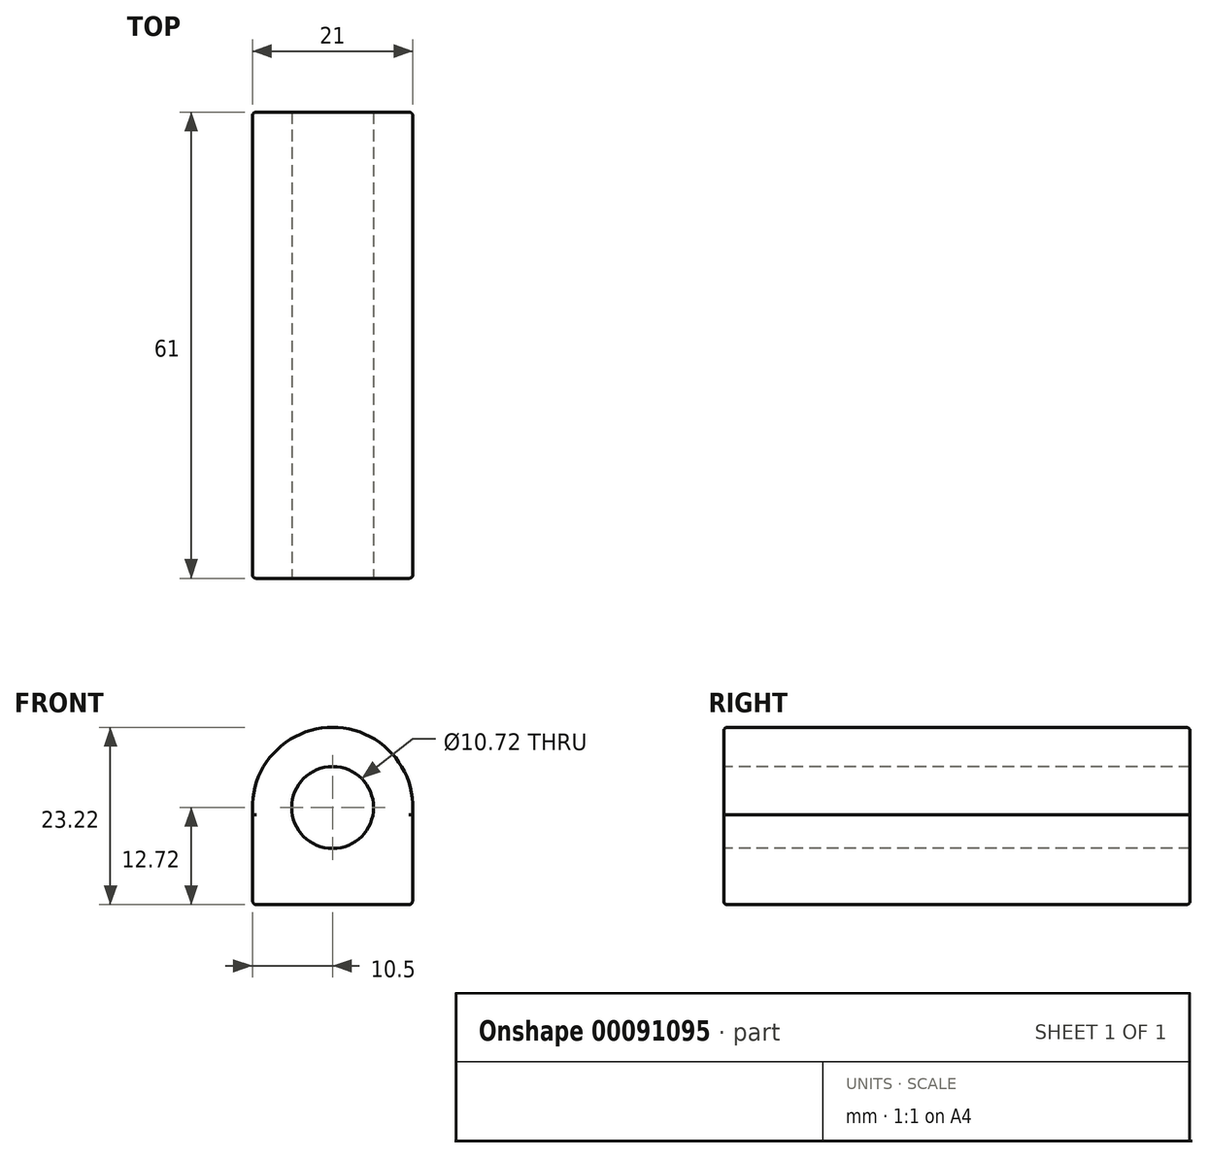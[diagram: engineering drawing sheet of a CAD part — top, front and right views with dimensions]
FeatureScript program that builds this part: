
annotation { "Feature Type Name" : "Feature", "Feature Type Description" : "" }
export const myFeature = defineFeature(function(context is Context, id is Id, definition is map)
    precondition{}
    {
        {
            var Q0;
            Q0=qCreatedBy(makeId("Front.planeOp"),FACE);
            var sketch = newSketch(context, id + "F0", { "sketchPlane" : qUnion([Q0])});
            skCircle(sketch, "E0", {"center": v(0, 0) * mm, "radius": 10.5 * mm});
            skLineSegment(sketch, "E1", {"start": v(0, 0) * mm, "end": v(0, -10.5) * mm, "construction": true});
            skLineSegment(sketch, "E2", {"start": v(0, -5.25) * mm, "end": v(-9.1, -5.25) * mm, "construction": true});
            skLineSegment(sketch, "E3.bottom", {"start": v(10.46, -10.72) * mm, "end": v(-10.46, -10.72) * mm});
            skLineSegment(sketch, "E3.top", {"start": v(10.46, 0.22) * mm, "end": v(-10.46, 0.22) * mm});
            skLineSegment(sketch, "E3.left", {"start": v(10.46, -10.72) * mm, "end": v(10.46, 0.22) * mm});
            skLineSegment(sketch, "E3.right", {"start": v(-10.46, -10.72) * mm, "end": v(-10.46, 0.22) * mm});
            skPoint(sketch, "E3.middle", {"position": v(0, -5.25) * mm});
            skSolve(sketch);
        }
        {
            var Q0;
            {var subQ5=sQuery(id+"F0.wireOp",EDGE,"E3.top");Q0=makeQuery(id+"F0.imprint","IMPRINT",FACE,{"disambiguationData":[TD([[makeQuery(id+"F0.imprint","IMPRINT",EDGE,{"derivedFrom":subQ5}),-1.0]])]});}
            var sketch = newSketch(context, id + "F1", { "sketchPlane" : qUnion([Q0])});
            skCircle(sketch, "E4", {"center": v(0, 0) * mm, "radius": 5.36 * mm});
            skSolve(sketch);
        }
        {
            var Q0;
            Q0 = qSketchRegion(id + "F1", true);
            var Q1;
            {var subQ5=sQuery(id+"F0.wireOp",EDGE,"E3.top");Q1=makeQuery(id+"F0.imprint","IMPRINT",FACE,{"disambiguationData":[TD([[makeQuery(id+"F0.imprint","IMPRINT",EDGE,{"derivedFrom":subQ5}),-1.0]])]});}
            var Q2;
            {var subQ5=sQuery(id+"F0.wireOp",EDGE,"E3.top");Q2=makeQuery(id+"F0.imprint","IMPRINT",FACE,{"disambiguationData":[TD([[makeQuery(id+"F0.imprint","IMPRINT",EDGE,{"derivedFrom":subQ5}),1.0]])]});}
            var Q3;
            {var subQ5=sQuery(id+"F0.wireOp",EDGE,"E3.bottom");Q3=makeQuery(id+"F0.imprint","IMPRINT",FACE,{"disambiguationData":[TD([[makeQuery(id+"F0.imprint","IMPRINT",EDGE,{"derivedFrom":subQ5}),-1.0]])]});}
            extrude(context, id + "F2", {"entities" : qUnion([Q0, Q1, Q2, Q3]), "flatOperationType" : FlatOperationType.REMOVE, "offsetDistance" : 25 * mm, "depth" : 61 * mm, "domain" : OperationDomain.MODEL});
        }
        {
            var Q0;
            Q0=makeQuery(id+"F2.opExtrude","CAP_FACE",FACE,{"disambiguationData":[OSD([sQuery(id+"F1.wireOp",EDGE,"E4")])],"isStart":false});
            extrude(context, id + "F3", {"entities" : qUnion([Q0]), "operationType" : NewBodyOperationType.REMOVE, "endBound" : BoundingType.THROUGH_ALL, "oppositeDirection" : true, "depth" : 25 * mm});
        }
        {
            var Q0;
            Q0=makeQuery(id+"F2.opExtrude","SWEPT_FACE",FACE,{"disambiguationData":[OSD([sQuery(id+"F0.wireOp",EDGE,"E3.bottom")])]});
            extrude(context, id + "F4", {"entities" : qUnion([Q0]), "operationType" : NewBodyOperationType.ADD, "depth" : 2 * mm});
        }
        {
            var Q0;
            Q0=makeQuery(id+"F2.opExtrude","CAP_EDGE",EDGE,{"disambiguationData":[OSD([sQuery(id+"F0.wireOp",EDGE,"E0")])],"isStart":false});
            var Q1;
            Q1=makeQuery(id+"F2.opExtrude","CAP_EDGE",EDGE,{"disambiguationData":[OSD([sQuery(id+"F0.wireOp",EDGE,"E3.right")])],"isStart":false});
            var Q2;
            Q2=makeQuery(id+"F2.opExtrude","CAP_EDGE",EDGE,{"disambiguationData":[OSD([sQuery(id+"F0.wireOp",EDGE,"E3.left")])],"isStart":false});
            var Q3;
            Q3=makeQuery(id+"F2.opExtrude","CAP_EDGE",EDGE,{"disambiguationData":[OSD([sQuery(id+"F0.wireOp",EDGE,"E3.bottom")])],"isStart":false});
            var Q4;
            Q4=makeQuery(id+"F2.opExtrude","CAP_EDGE",EDGE,{"disambiguationData":[OSD([sQuery(id+"F0.wireOp",EDGE,"E3.bottom")])],"isStart":true});
            var Q5;
            Q5=makeQuery(id+"F2.opExtrude","CAP_EDGE",EDGE,{"disambiguationData":[OSD([sQuery(id+"F0.wireOp",EDGE,"E3.left")])],"isStart":true});
            var Q6;
            Q6=makeQuery(id+"F2.opExtrude","CAP_EDGE",EDGE,{"disambiguationData":[OSD([sQuery(id+"F0.wireOp",EDGE,"E3.right")])],"isStart":true});
            var Q7;
            Q7=makeQuery(id+"F2.opExtrude","CAP_EDGE",EDGE,{"disambiguationData":[OSD([sQuery(id+"F0.wireOp",EDGE,"E0")])],"isStart":true});
            var Q8;
            Q8=makeQuery(id+"F2.opExtrude","SWEPT_EDGE",EDGE,{"disambiguationData":[OSD([sQuery(id+"F0.wireOp",EDGE,"E3.bottom"),sQuery(id+"F0.wireOp",EDGE,"E3.right")])]});
            var Q9;
            Q9=makeQuery(id+"F2.opExtrude","SWEPT_EDGE",EDGE,{"disambiguationData":[OSD([sQuery(id+"F0.wireOp",EDGE,"E3.bottom"),sQuery(id+"F0.wireOp",EDGE,"E3.left")])]});
            fillet(context, id + "F5", {"entities" : qUnion([Q0, Q1, Q2, Q3, Q4, Q5, Q6, Q7, Q8, Q9]), "radius" : .5 * mm, "tangentPropagation" : true, "allowEdgeOverflow" : false});
        }
        {
            var Q0;
            Q0=makeQuery(id+"F4.opExtrude","CAP_EDGE",EDGE,{"disambiguationData":[OSD([sQuery(id+"F0.wireOp",EDGE,"E3.bottom"),sQuery(id+"F0.wireOp",EDGE,"E3.left")])],"isStart":false});
            var Q1;
            {var subQ0=sQuery(id+"F0.wireOp",EDGE,"E3.bottom");Q1=makeQuery(id+"F4.opExtrude","CAP_EDGE",EDGE,{"disambiguationData":[OSD([subQ0]),TDD([makeQuery(id+"F2.opExtrude","CAP_EDGE",EDGE,{"disambiguationData":[OSD([subQ0])],"isStart":true})])],"isStart":false});}
            var Q2;
            {var subQ0=sQuery(id+"F0.wireOp",EDGE,"E3.bottom");Q2=makeQuery(id+"F4.opExtrude","CAP_EDGE",EDGE,{"disambiguationData":[OSD([subQ0]),TDD([makeQuery(id+"F2.opExtrude","CAP_EDGE",EDGE,{"disambiguationData":[OSD([subQ0])],"isStart":false})])],"isStart":false});}
            var Q3;
            Q3=makeQuery(id+"F4.opExtrude","CAP_EDGE",EDGE,{"disambiguationData":[OSD([sQuery(id+"F0.wireOp",EDGE,"E3.bottom"),sQuery(id+"F0.wireOp",EDGE,"E3.right")])],"isStart":false});
            fillet(context, id + "F6", {"entities" : qUnion([Q0, Q1, Q2, Q3]), "radius" : .5 * mm, "tangentPropagation" : true, "allowEdgeOverflow" : false});
        }
    });
